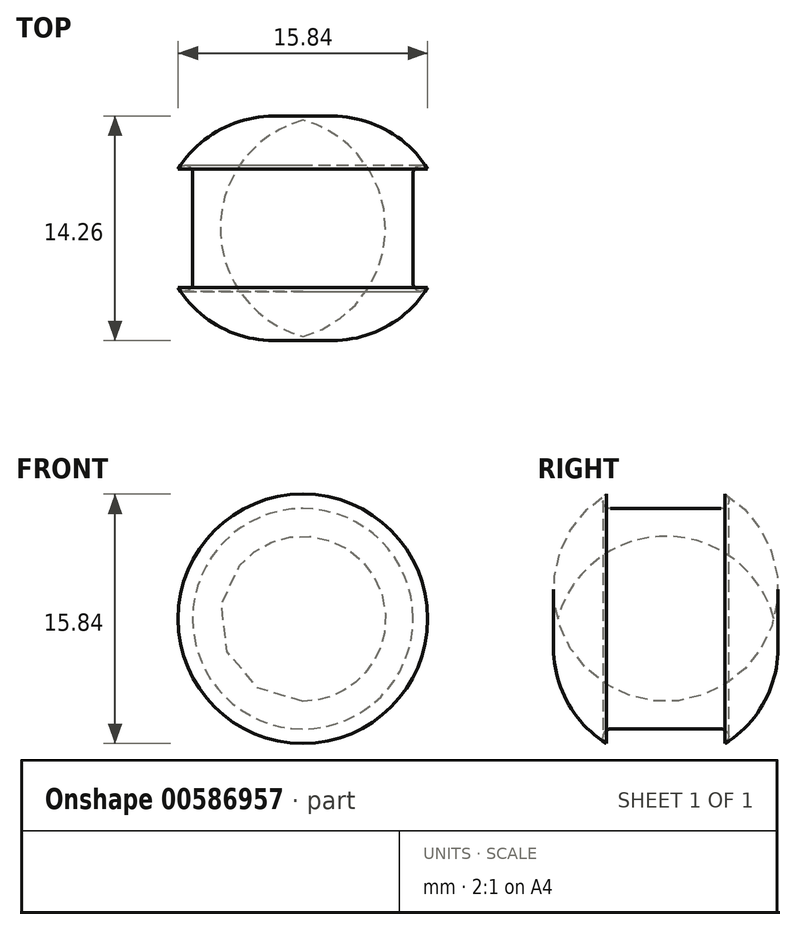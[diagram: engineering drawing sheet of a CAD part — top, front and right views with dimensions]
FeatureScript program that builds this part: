
annotation { "Feature Type Name" : "Feature", "Feature Type Description" : "" }
export const myFeature = defineFeature(function(context is Context, id is Id, definition is map)
    precondition{}
    {
        {
            var Q0;
            Q0=qCreatedBy(makeId("Right.planeOp"),FACE);
            var sketch = newSketch(context, id + "F0", { "sketchPlane" : qUnion([Q0])});
            skArc(sketch, "E0", {"start": v(0.26, 7.92) * mm, "mid": v(-3.5, 9) * mm, "end": v(-7.26, 7.92) * mm});
            skArc(sketch, "E1", {"start": v(0, 7) * mm, "mid": v(0.48, 7.36) * mm, "end": v(0.26, 7.92) * mm});
            skArc(sketch, "E2", {"start": v(-7.26, 7.92) * mm, "mid": v(-7.48, 7.36) * mm, "end": v(-7, 7) * mm});
            skLineSegment(sketch, "E3", {"start": v(-7, 7) * mm, "end": v(0, 7) * mm});
            skLineSegment(sketch, "E4", {"start": v(0, 0) * mm, "end": v(-9.6, 0) * mm});
            skSolve(sketch);
        }
        {
            var Q0;
            Q0=makeQuery(id+"F0.imprint","IMPRINT",FACE,{"disambiguationData":[TD([[makeQuery(id+"F0.imprint","IMPRINT",EDGE,{"derivedFrom":sQuery(id+"F0.wireOp",EDGE,"E0")}),1.0]])]});
            var Q1;
            Q1=sQuery(id+"F0.wireOp",EDGE,"E4");
            revolve(context, id + "F1", {"entities" : qUnion([Q0]), "axis" : qUnion([Q1]), "revolveType" : RevolveType.FULL});
        }
    });
